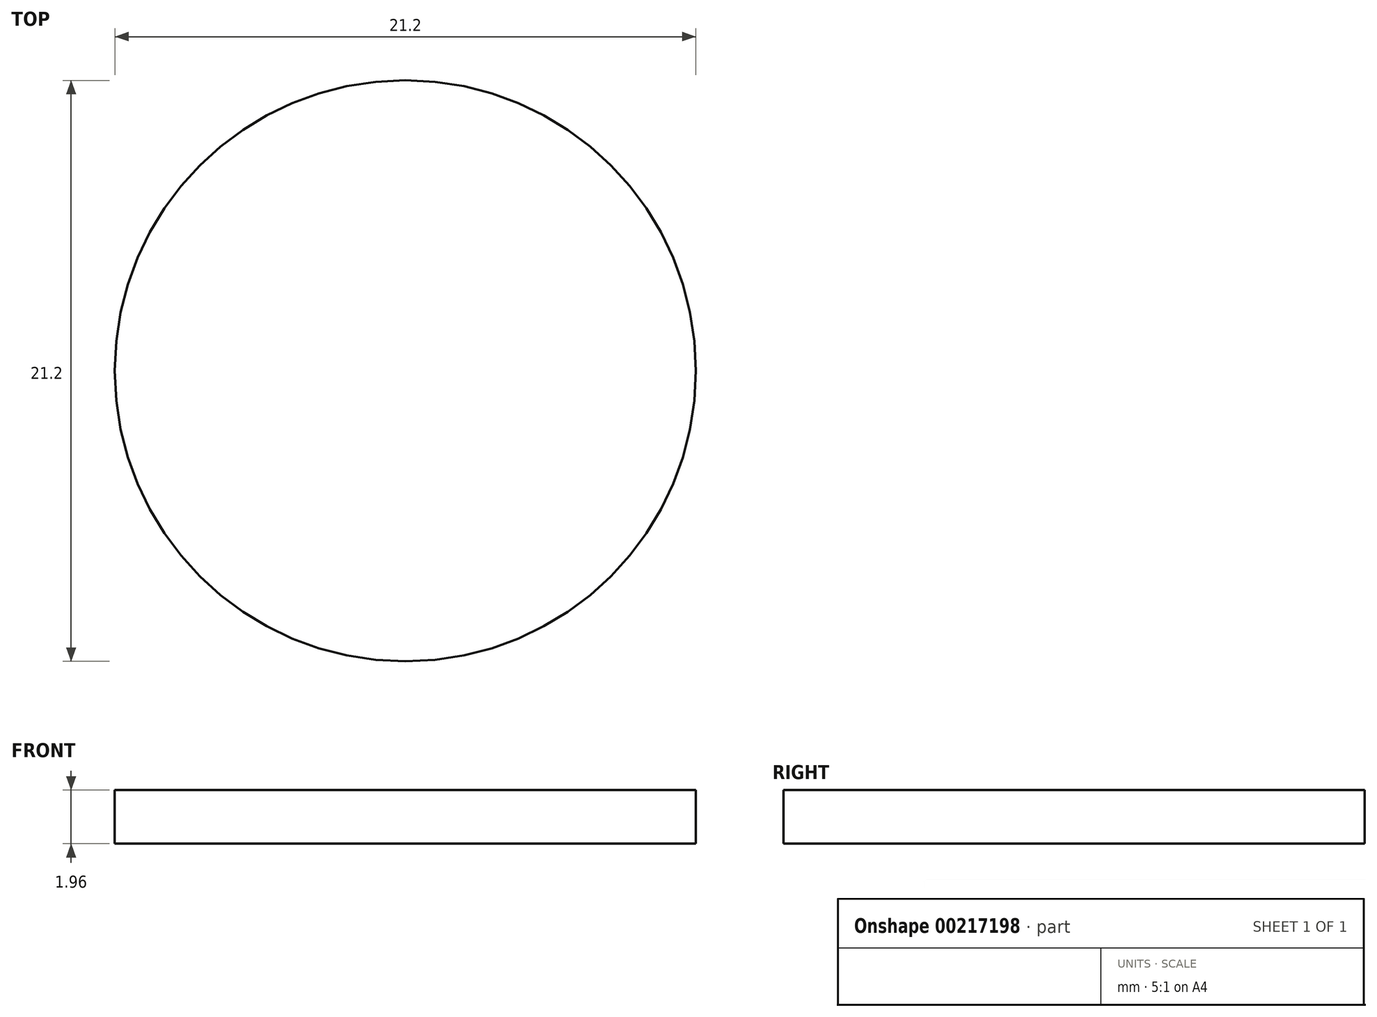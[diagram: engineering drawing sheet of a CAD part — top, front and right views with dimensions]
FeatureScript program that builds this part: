
annotation { "Feature Type Name" : "Feature", "Feature Type Description" : "" }
export const myFeature = defineFeature(function(context is Context, id is Id, definition is map)
    precondition{}
    {
        {
            var Q0;
            Q0=qCreatedBy(makeId("Top.planeOp"),FACE);
            var sketch = newSketch(context, id + "F0", { "sketchPlane" : qUnion([Q0])});
            skCircle(sketch, "E0", {"center": v(0, 0) * mm, "radius": 10.6 * mm});
            skSolve(sketch);
        }
        {
            var Q0;
            Q0=qSketchRegion(id+"F0",true);
            extrude(context, id + "F1", {"entities" : qUnion([Q0]), "endBound" : BoundingType.SYMMETRIC, "depth" : 1.95 * mm});
        }
    });
